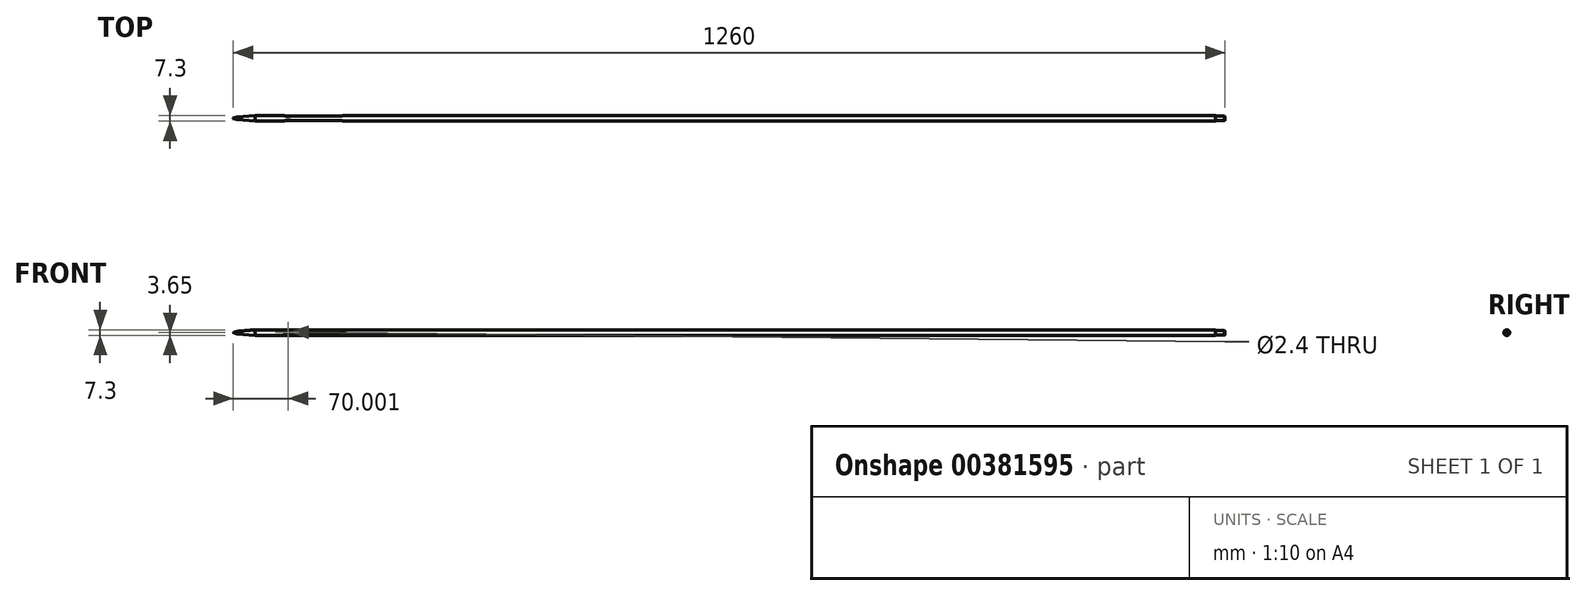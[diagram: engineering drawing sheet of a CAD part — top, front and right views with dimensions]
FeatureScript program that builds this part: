
annotation { "Feature Type Name" : "Feature", "Feature Type Description" : "" }
export const myFeature = defineFeature(function(context is Context, id is Id, definition is map)
    precondition{}
    {
        {
            var Q0;
            Q0=qCreatedBy(makeId("Right.planeOp"),FACE);
            var sketch = newSketch(context, id + "F0", { "sketchPlane" : qUnion([Q0])});
            skCircle(sketch, "E0", {"center": v(0, 0) * mm, "radius": 3.65 * mm});
            skSolve(sketch);
        }
        {
            var Q0;
            Q0=qSketchRegion(id+"F0",true);
            extrude(context, id + "F1", {"entities" : qUnion([Q0]), "depth" : 1220 * mm});
        }
        {
            var Q0;
            Q0=makeQuery(id+"F1.opExtrude","CAP_FACE",FACE,{"disambiguationData":[OSD([sQuery(id+"F0.wireOp",EDGE,"E0")])],"isStart":false});
            var sketch = newSketch(context, id + "F2", { "sketchPlane" : qUnion([Q0])});
            skCircle(sketch, "E1", {"center": v(0, 0) * mm, "radius": 3 * mm});
            skSolve(sketch);
        }
        {
            var Q0;
            Q0=qSketchRegion(id+"F2",true);
            extrude(context, id + "F3", {"entities" : qUnion([Q0]), "operationType" : NewBodyOperationType.ADD, "depth" : 12 * mm});
        }
        {
            var Q0;
            Q0=makeQuery(id+"F3.opExtrude","CAP_EDGE",EDGE,{"disambiguationData":[OSD([sQuery(id+"F2.wireOp",EDGE,"E1")])],"isStart":false});
            chamfer(context, id + "F4", {"entities" : qUnion([Q0]), "width" : .75 * mm, "tangentPropagation" : true});
        }
        {
            var Q0;
            Q0=makeQuery(id+"F1.opExtrude","CAP_FACE",FACE,{"disambiguationData":[OSD([sQuery(id+"F0.wireOp",EDGE,"E0")])],"isStart":true});
            var sketch = newSketch(context, id + "F5", { "sketchPlane" : qUnion([Q0])});
            skCircle(sketch, "E2", {"center": v(0, 0) * mm, "radius": 4.12 * mm});
            skSolve(sketch);
        }
        {
            var Q0;
            Q0=makeQuery(id+"F5.imprint","IMPRINT",FACE,{"disambiguationData":[TD([[makeQuery(id+"F5.imprint","IMPRINT",EDGE,{"derivedFrom":makeQuery(id+"F1.opExtrude","CAP_EDGE",EDGE,{"disambiguationData":[OSD([sQuery(id+"F0.wireOp",EDGE,"E0")])],"isStart":true})}),-1.0]])]});
            extrude(context, id + "F6", {"entities" : qUnion([Q0]), "operationType" : NewBodyOperationType.ADD, "depth" : 23 * mm, "hasDraft" : true, "draftAngle" : 5 * degree, "draftPullDirection" : true});
        }
        {
            var Q0;
            Q0=makeQuery(id+"F6.opExtrude","CAP_FACE",FACE,{"disambiguationData":[OSD([sQuery(id+"F0.wireOp",EDGE,"E0")])],"isStart":false});
            var sketch = newSketch(context, id + "F7", { "sketchPlane" : qUnion([Q0])});
            skCircle(sketch, "E3", {"center": v(0, 0) * mm, "radius": 1.64 * mm});
            skSolve(sketch);
        }
        {
            var Q0;
            Q0=makeQuery(id+"F7.imprint","IMPRINT",FACE,{"disambiguationData":[TD([[makeQuery(id+"F7.imprint","IMPRINT",EDGE,{"derivedFrom":makeQuery(id+"F6.opExtrude","CAP_EDGE",EDGE,{"disambiguationData":[OSD([sQuery(id+"F0.wireOp",EDGE,"E0")])],"isStart":false})}),-1.0]])]});
            extrude(context, id + "F8", {"entities" : qUnion([Q0]), "operationType" : NewBodyOperationType.ADD, "depth" : 5 * mm, "hasDraft" : true, "draftAngle" : 18 * degree, "draftPullDirection" : true});
        }
        {
            var Q0;
            Q0=makeQuery(id+"F1.opExtrude","SWEPT_BODY",BODY,{"disambiguationData":[OSD([sQuery(id+"F0.wireOp",EDGE,"E0")])]});
            var Q1;
            Q1=makeQuery(id+"F6.opExtrude","SWEPT_BODY",BODY,{"disambiguationData":[OSD([sQuery(id+"F0.wireOp",EDGE,"E0")])]});
            transform(context, id + "F9", {"entities" : qUnion([Q0, Q1]), "transformType" : TransformType.TRANSLATION_3D, "dx" : 28 * mm, "dy" : 0 * mm, "dz" : 0 * mm, "makeCopy" : false});
        }
        {
            var Q0;
            Q0=qCreatedBy(makeId("Top.planeOp"),FACE);
            var sketch = newSketch(context, id + "F10", { "sketchPlane" : qUnion([Q0])});
            skLineSegment(sketch, "E4", {"start": v(65, 7.56) * mm, "end": v(65, -10.12) * mm, "construction": true});
            skSolve(sketch);
        }
        {
            var Q0;
            Q0=qCreatedBy(makeId("Top.planeOp"),FACE);
            var sketch = newSketch(context, id + "F11", { "sketchPlane" : qUnion([Q0])});
            skLineSegment(sketch, "E5", {"start": v(142, 6.8) * mm, "end": v(142, -11.63) * mm, "construction": true});
            skSolve(sketch);
        }
        {
            var Q0;
            Q0=qCreatedBy(makeId("Top.planeOp"),FACE);
            var sketch = newSketch(context, id + "F12", { "sketchPlane" : qUnion([Q0])});
            skPoint(sketch, "E6.middle", {"position": v(65.03, 0) * mm});
            skLineSegment(sketch, "E7.bottom", {"start": v(141.96, 3.1) * mm, "end": v(64.96, 3.1) * mm});
            skLineSegment(sketch, "E7.top", {"start": v(141.96, -3.1) * mm, "end": v(64.96, -3.1) * mm});
            skLineSegment(sketch, "E7.left", {"start": v(141.96, 3.1) * mm, "end": v(141.96, -3.1) * mm});
            skLineSegment(sketch, "E7.right", {"start": v(64.96, 3.1) * mm, "end": v(64.96, -3.1) * mm});
            skPoint(sketch, "E7.middle", {"position": v(103.46, 0) * mm});
            skSolve(sketch);
        }
        {
            var Q0;
            Q0=qCreatedBy(makeId("Top.planeOp"),FACE);
            var sketch = newSketch(context, id + "F13", { "sketchPlane" : qUnion([Q0])});
            skLineSegment(sketch, "E8", {"start": v(138, 7.3) * mm, "end": v(138, -12.2) * mm, "construction": true});
            skSolve(sketch);
        }
        {
            var Q0;
            Q0=qCreatedBy(makeId("Top.planeOp"),FACE);
            var sketch = newSketch(context, id + "F14", { "sketchPlane" : qUnion([Q0])});
            skLineSegment(sketch, "E9.bottom", {"start": v(65, 3.1) * mm, "end": v(138, 3.1) * mm});
            skLineSegment(sketch, "E9.top", {"start": v(65, 11.8) * mm, "end": v(138, 11.8) * mm});
            skLineSegment(sketch, "E9.left", {"start": v(65, 3.1) * mm, "end": v(65, 11.8) * mm});
            skLineSegment(sketch, "E9.right", {"start": v(138, 3.1) * mm, "end": v(138, 11.8) * mm});
            skLineSegment(sketch, "E10.bottom", {"start": v(65, -8.52) * mm, "end": v(138, -8.52) * mm});
            skLineSegment(sketch, "E10.top", {"start": v(65, -3.1) * mm, "end": v(138, -3.1) * mm});
            skLineSegment(sketch, "E10.left", {"start": v(65, -8.52) * mm, "end": v(65, -3.1) * mm});
            skLineSegment(sketch, "E10.right", {"start": v(138, -8.52) * mm, "end": v(138, -3.1) * mm});
            skSolve(sketch);
        }
        {
            var Q0;
            Q0 = qSketchRegion(id + "F14", true);
            extrude(context, id + "F15", {"entities" : qUnion([Q0]), "operationType" : NewBodyOperationType.REMOVE, "oppositeDirection" : true, "depth" : 25 * mm, "hasSecondDirection" : true, "secondDirectionOppositeDirection" : false, "secondDirectionDepth" : 25 * mm});
        }
        {
            var Q0;
            Q0=qCreatedBy(makeId("Front.planeOp"),FACE);
            var sketch = newSketch(context, id + "F16", { "sketchPlane" : qUnion([Q0])});
            skCircle(sketch, "E11", {"center": v(70, 0) * mm, "radius": 1.2 * mm});
            skSolve(sketch);
        }
        {
            var Q0;
            Q0 = qSketchRegion(id + "F16", true);
            extrude(context, id + "F17", {"entities" : qUnion([Q0]), "operationType" : NewBodyOperationType.REMOVE, "oppositeDirection" : true, "depth" : 25 * mm, "hasSecondDirection" : true, "secondDirectionOppositeDirection" : false, "secondDirectionDepth" : 25 * mm});
        }
        {
            var Q0;
            Q0=qCreatedBy(makeId("Top.planeOp"),FACE);
            var sketch = newSketch(context, id + "F18", { "sketchPlane" : qUnion([Q0])});
            skLineSegment(sketch, "E12", {"start": v(138, -3.1) * mm, "end": v(142, -3.65) * mm});
            skLineSegment(sketch, "E13", {"start": v(142.03, -3.65) * mm, "end": v(142.23, -3.65) * mm, "construction": true});
            skSolve(sketch);
        }
        {
            var Q0;
            Q0=qCreatedBy(makeId("Top.planeOp"),FACE);
            var sketch = newSketch(context, id + "F19", { "sketchPlane" : qUnion([Q0])});
            skLineSegment(sketch, "E14", {"start": v(138, -3.1) * mm, "end": v(142, -3.65) * mm});
            skLineSegment(sketch, "E15", {"start": v(142, -3.65) * mm, "end": v(142, -4.27) * mm});
            skLineSegment(sketch, "E16", {"start": v(142, -4.27) * mm, "end": v(138, -4.27) * mm});
            skLineSegment(sketch, "E17", {"start": v(138, -4.27) * mm, "end": v(138, -3.1) * mm});
            skLineSegment(sketch, "E18", {"start": v(138, 3.1) * mm, "end": v(142, 3.65) * mm});
            skLineSegment(sketch, "E19", {"start": v(142, 3.65) * mm, "end": v(142, 4.31) * mm});
            skLineSegment(sketch, "E20", {"start": v(142, 4.31) * mm, "end": v(138, 4.31) * mm});
            skLineSegment(sketch, "E21", {"start": v(138, 4.31) * mm, "end": v(138, 3.1) * mm});
            skSolve(sketch);
        }
        {
            var Q0;
            Q0=makeQuery(id+"F19.imprint","IMPRINT",FACE,{"disambiguationData":[TD([[makeQuery(id+"F19.imprint","IMPRINT",EDGE,{"derivedFrom":sQuery(id+"F19.wireOp",EDGE,"E14")}),-1.0]])]});
            var Q1;
            Q1=makeQuery(id+"F19.imprint","IMPRINT",FACE,{"disambiguationData":[TD([[makeQuery(id+"F19.imprint","IMPRINT",EDGE,{"derivedFrom":sQuery(id+"F19.wireOp",EDGE,"E18")}),1.0]])]});
            extrude(context, id + "F20", {"entities" : qUnion([Q0, Q1]), "operationType" : NewBodyOperationType.REMOVE, "oppositeDirection" : true, "depth" : 25 * mm, "hasSecondDirection" : true, "secondDirectionOppositeDirection" : false, "secondDirectionDepth" : 25 * mm});
        }
    });
